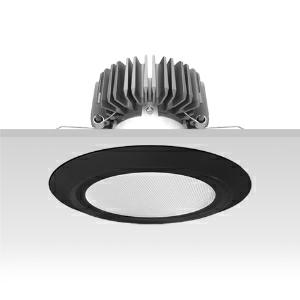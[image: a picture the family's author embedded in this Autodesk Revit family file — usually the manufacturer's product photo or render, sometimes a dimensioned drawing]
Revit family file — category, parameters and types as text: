
# Revit family: 3f_filippi_-_3f_reno_bianco_ampio_3f_filippi_-_30646_a01038_-_3f_reno_200_wh_2000-840_ep_wide___vs_bk_4e39
name_source: partatom
category: Lighting Fixtures
units: mm (PartAtom-declared; Revit-internal decimal feet)

## family parameters
Cut with Voids When Loaded = No
Host = Face
Light Source = No
Part Type = Normal
Room Calculation Point = No
Round Connector Dimension = Use Diameter
Shared = No

## types (1)
- 3F Filippi - 3F Reno Bianco Ampio (1 x LED, 1723 lm, 21 W, 4000 K)
    Apparent Load = 21 VA
    Approval mark = ENEC
    CIE Flux Codes = 75 94 99 100 100
    Color Rendering = 80
    Color Temperature = 4000 K
    Control Gear = Electronic ballast
    Default Elevation = 1800 mm
    Description = ILLUMINOTECHNICAL
Luminous efficiency 100% (DLOR 100%, ULOR 0%).
Initial luminous flux of the luminaire 1723 lm.
Emergency luminaire luminous flux BLF 20%.
Direct symmetric wide distribution.
Installation Interdistance Transv.D = 1.16 x hu - Long.D = 1.14 x hu.
Average luminance <3000 cd/m² for radial angles >65°.
Tabular UGR (CIE 117 - 4H-8H; S=0.25H; 70/50/20): RUG 20.4 - 20.3.
Beam angle: 74° - 74°.
Luminous efficacy 82 lm/W.
Lifetime (L90/B10): 30000 h. (tq+25°C)
Lifetime (L85/B10): 50000 h. (tq+25°C)
Lifetime (L70/B10): 80000 h. (tq+25°C)
Sudden decreased luminous flux after 50000 hours: 0% (C0).
Photobiological safety in compliance with IEC/TR 62778: RG0 risk exempt, (IEC 62471).
In compliance with IEC/EN 62722-2-1 - IEC/EN 62717 standards.

SOURCE
Compact LED module 2000/840.
Energy efficiency class (UE 2019/2020 - UE 2019/2015): D.
CIE 13.3 Colour rendering index: CRI >80 (R9 <50%).
IES TM-30 Fidelity Index: Rf = 84 Rg = 95.
CCT nominal colour temperature 4000 K.
Colour initial tolerance (MacAdam): SDCM 3.
Zhaga Book 3 compliant.

MECHANICAL
Passive heat dissipator in die-casting aluminium, oversized, for optimum thermal management of the LED module.
Parabolic element with graduated/concentric rings in white polycarbonate.
Transparent external lens with glossy and satin differentiated surfaces, with a cooling and anti-insect system in methacrylate (PMMA).
Fastening spring clips in stainless steel.
Dimensions: diameter 226 mm, height 146 mm. Weight 1.605 kg.
IP44 protection degree for exposed part, IP20 for recessed part.
Mechanical strength to impacts IK06 (1 joule).
Glow-wire test resistance 650°C.

ELECTRICAL
Wiring on a separate unit.
Halogen Free electronic wiring 230V-50/60Hz, power factor 0.90, THD <25%, constant output current, SELV, class II, 1 driver.
Power of the luminaire 21 W.
CE - IEC 60598-1 - EN 60598-1.
EP maintained emergency wiring on board, 1h duration, 24h recharge; compliant with EN 60598-2-22, excluding high risk areas.
SAFE FLICKER: PstLM=<1 and SVM=<0.4 (IEC TR 61547-1 and IEC TR 63158), to ensure a more comfortable and safe light.
Ambient temperature from +5°C to +25°C.
Temperature class T6 max 85°C.
Relative humidity UR: <85%.

INSTALLATION
Pull-up recessed fitting.
False ceiling carving: 200 mm.
All accessories dedicated to this product are available on the Catalog and on our website www.3F-Filippi.com.

ACCESSORIES
A01038 - Anti-glare microprismatic VS moulded glass, tempered, not flammable, locked and in line with the trim, in black polycarbonate.

APPLICATIONS
Environments: architectural, commercial, exhibition areas, transit areas, corridors, shops, display windows, service areas.
In false ceilings with narrow voids.

WARNING
Luminaire designed for disposal/recycling at end-of-life.
Replaceable (LED only) light source by a professional. Replaceable control gear by a professional.
    Height = 0 mm  [stored 0 ft]
    Lamp = 1 x LED
    Lamp Light Flux = 1723 lm
    Lamp Power = 21 W
    Lamp count = 1
    Length = 226 mm
    Lifetime = 50000 h
    Luminous efficacy = 82 lm/W
    Manufacturer = 3F Filippi
    ModVariant = No
    Model = 3F Filippi - 30646+A01038 - 3F Reno 200 WH 2000-840 EP WIDE + VS BK
    Mounting Place = Ceiling
    Mounting Type = Recessed
    Number of Poles = 1
    OnlyDefault = Yes
    Power Factor = 1
    Product Name = 3F Filippi - 3F Reno Bianco Ampio
    Product group = recessed luminaire
    ProductGroupID = 4
    Protection Class = Protection class II
    Protection Degree = IP 20
    RLX_Detail_Level = 1
    RLX_Emergency_Light_Flux = 0 lm
    RLX_Emergency_Type = 0
    RLX_Emergency_Type_DB = No
    RlxData = <blob elided: 96845 chars, md5=f4e5f8cf>
    Socket = socket
    Standby Power = 0 W
    System Light Flux = 1723 lm
    System Power = 21 W
    Type Comments = Product without accessories
    Type Image = 3ffilippi_3f_reno_200_bk_vs_smp.jpg
    URL = http://relux.com
    VarID = ---
    Voltage = 0 V
    Weight = 0.00 kg
    Width = 0 mm  [stored 0 ft]

note: [stored X ft] marks values corroborated as IEEE doubles in the binary element streams (Revit-internal decimal feet)

## geometry (parser evidence)
native form markers: Blend x4, Sweep x9
no freeform markers — native parametric forms only
